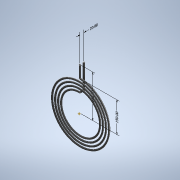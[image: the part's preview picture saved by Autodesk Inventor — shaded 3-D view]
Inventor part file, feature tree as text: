
AUTODESK INVENTOR PART (.ipt)
format: ipt  version: 2022.1 (Build 261234000, 234)  size: 363,520 bytes
history: native  units: mm
features: sketch x6, extrude x6, other x5, revolve x1, sweep x1
ambient origin geometry x8: Origin, YZ Plane, XZ Plane, XY Plane, X Axis, Y Axis, Z Axis, Center Point
bodies: Solid3 (feature_tree), Solid4 (feature_tree)
feature tree (19):
  other  "Annotations"
  sketch  "3D Sketch1"
  sketch  "Sketch1"  dims[d0=15.0mm d1=40.0mm d2=180.0mm d3=0.0mm]
  sketch  "Sketch3"  dims[d7=8.0mm d8=10.0mm d9=0.0mm]
  extrude  "Extrusion2"  TaperAngle=0.0deg  [1 undecoded]
  extrude  "Extrusion3"  Depth=10.0mm TaperAngle=0.0deg
  sketch  "Sketch4"  dims[d10=150.0mm d11=0.0mm d12=0.0mm d13=0.0mm]
  revolve  "Revolution1"  [1 undecoded]
  sweep  "Sweep1"
  extrude  "Extrusion4"  Depth=210.0mm TaperAngle=0.0deg
  extrude  "Extrusion5"  Depth=10.0mm TaperAngle=0.0deg
  sketch  "Sketch6"  dims[d17=20.0mm d18=0.0mm d20=210.0mm d21=0.0mm d22=10.0mm d23=0.0mm d19=210.0mm d24=200.639993mm d25=20.0mm d26=150.0mm]
  extrude  "Extrusion6"  Depth=210.0mm
  extrude  "Extrusion7"  [1 undecoded]
  other  "Helical Curve1"
  sketch  "Sketch5"  dims[d14=360.0deg d15=60.0mm d16=0.0mm]
  other  "Linear Dimension 1"
  other  "Linear Dimension 2"
  other  "Linear Dimension 3"
note: 3 required parameter values undecoded (feature->parameter linkage not recoverable at this tier; creation-order binding heuristic only, values carry confidence <= 0.55)